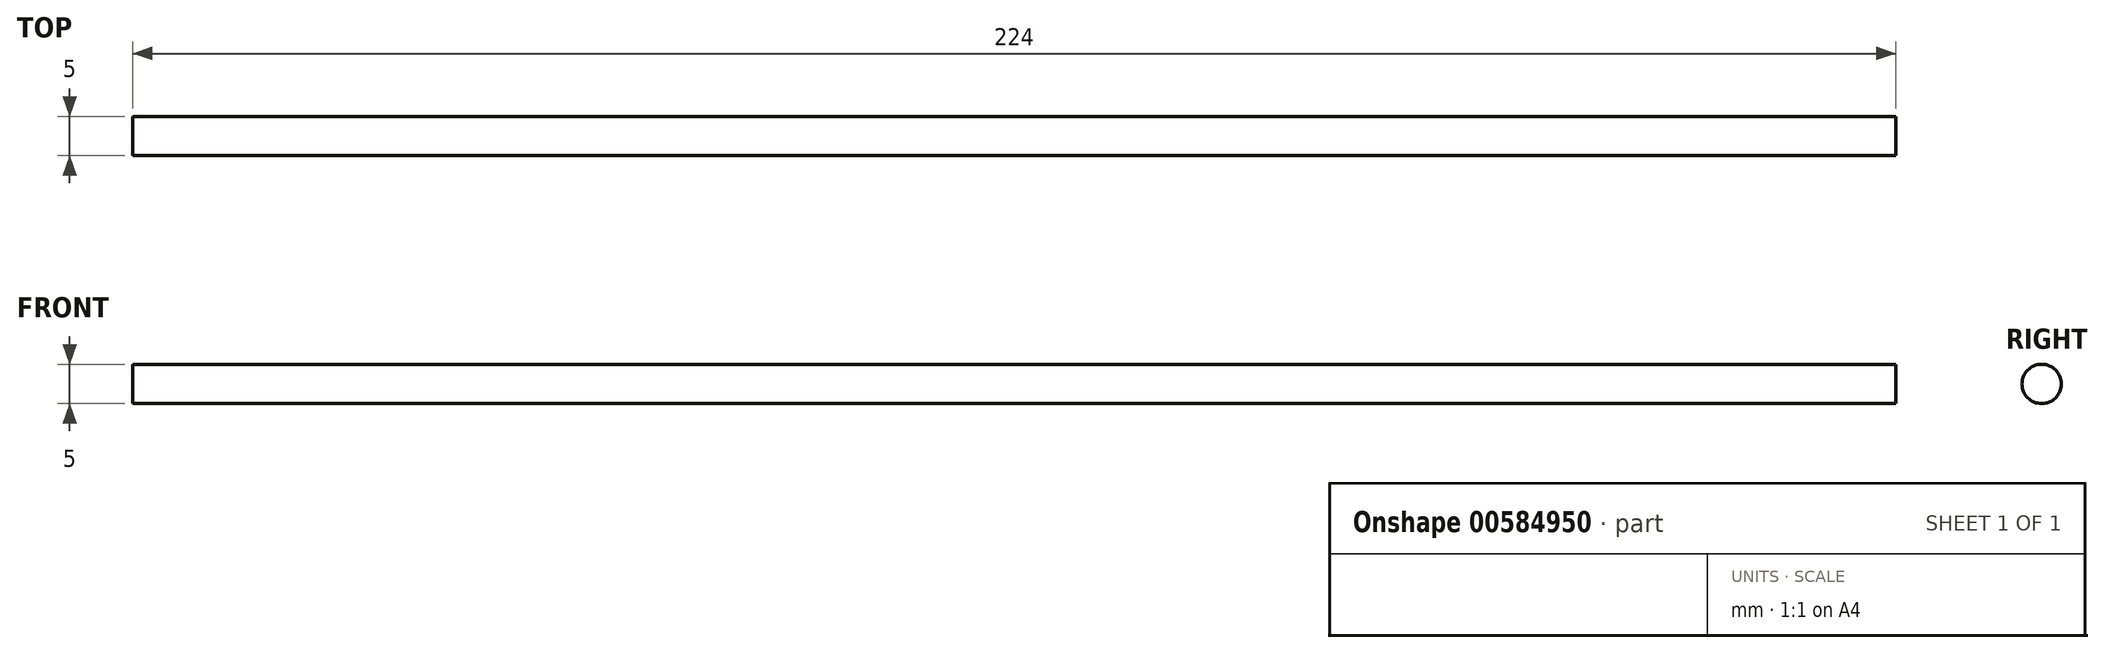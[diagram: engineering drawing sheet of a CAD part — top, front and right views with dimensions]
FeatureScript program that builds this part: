
annotation { "Feature Type Name" : "Feature", "Feature Type Description" : "" }
export const myFeature = defineFeature(function(context is Context, id is Id, definition is map)
    precondition{}
    {
        {
            var Q0;
            Q0=qCreatedBy(makeId("Right.planeOp"),FACE);
            var sketch = newSketch(context, id + "F0", { "sketchPlane" : qUnion([Q0])});
            skCircle(sketch, "E0", {"center": v(0, 0) * mm, "radius": 2.5 * mm});
            skSolve(sketch);
        }
        {
            var Q0;
            Q0=makeQuery(id+"F0.imprint","IMPRINT",FACE,{"disambiguationData":[TD([[makeQuery(id+"F0.imprint","IMPRINT",EDGE,{"derivedFrom":sQuery(id+"F0.wireOp",EDGE,"E0")}),1.0]])]});
            extrude(context, id + "F1", {"entities" : qUnion([Q0]), "depth" : 224 * mm, "offsetDistance" : 25 * mm});
        }
    });
